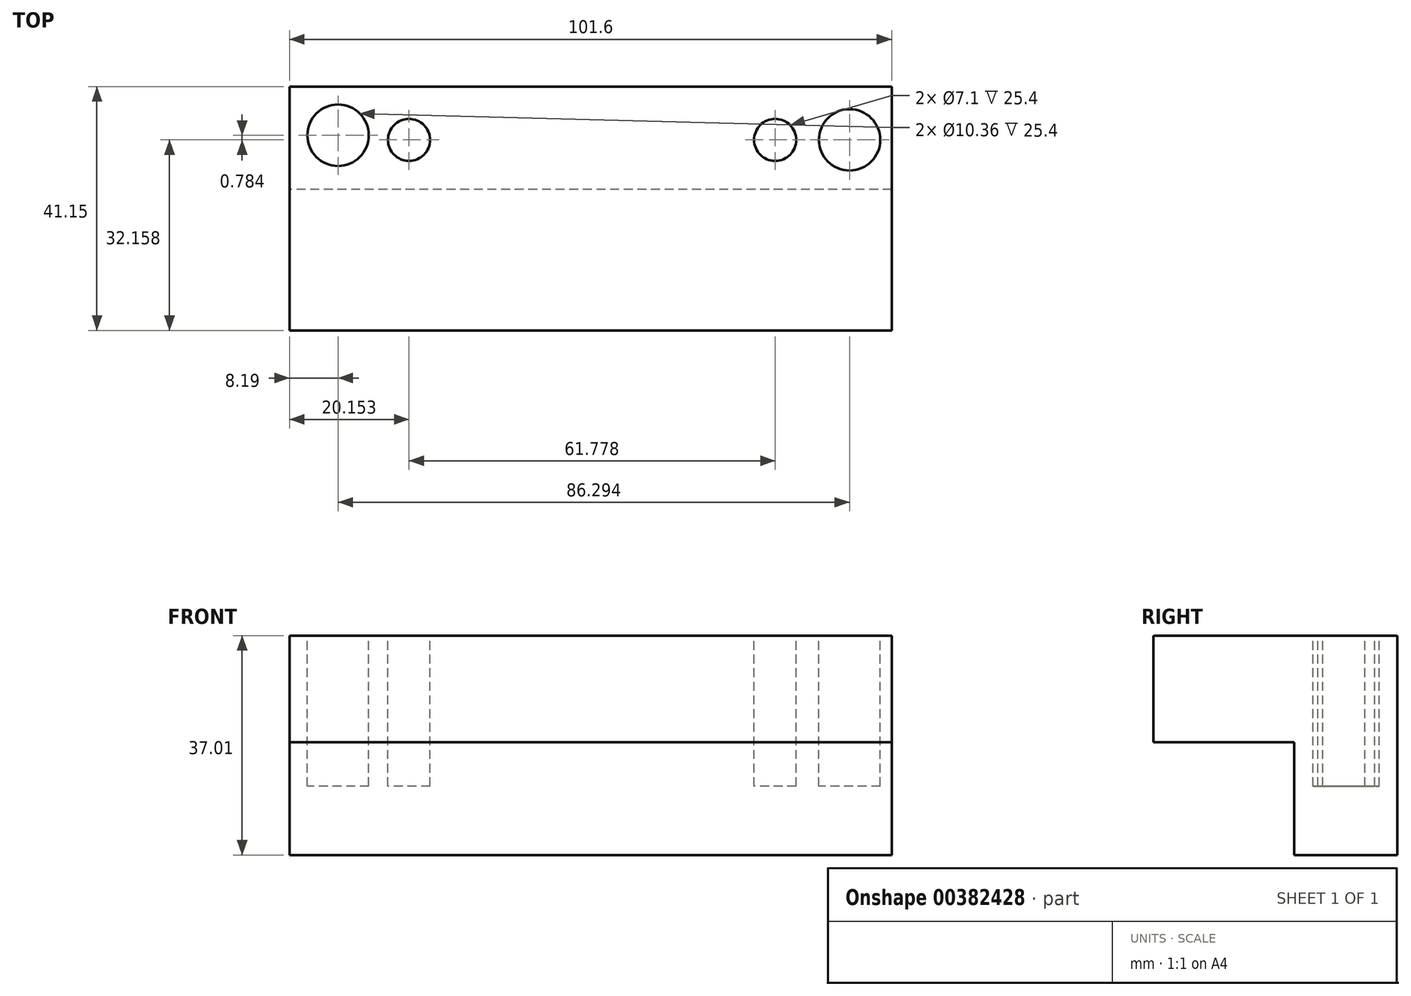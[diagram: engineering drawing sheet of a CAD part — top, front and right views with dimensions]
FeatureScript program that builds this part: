
annotation { "Feature Type Name" : "Feature", "Feature Type Description" : "" }
export const myFeature = defineFeature(function(context is Context, id is Id, definition is map)
    precondition{}
    {
        {
            var Q0;
            Q0=qCreatedBy(makeId("Right.planeOp"),FACE);
            var sketch = newSketch(context, id + "F0", { "sketchPlane" : qUnion([Q0])});
            skLineSegment(sketch, "E0", {"start": v(0, 0) * mm, "end": v(0, -19.05) * mm});
            skLineSegment(sketch, "E1", {"start": v(0, -19.05) * mm, "end": v(-17.37, -19.05) * mm});
            skLineSegment(sketch, "E2", {"start": v(-17.37, -19.05) * mm, "end": v(-17.37, 0) * mm});
            skLineSegment(sketch, "E3", {"start": v(-17.37, 0) * mm, "end": v(-41.15, 0) * mm});
            skLineSegment(sketch, "E4", {"start": v(-41.15, 0) * mm, "end": v(-41.15, 8.43) * mm});
            skLineSegment(sketch, "E5", {"start": v(-28.45, 17.96) * mm, "end": v(0, 17.96) * mm});
            skLineSegment(sketch, "E6", {"start": v(0, 14.78) * mm, "end": v(0, -6.55) * mm});
            skPoint(sketch, "E7.visualSharp", {"position": v(0, 17.96) * mm});
            skPoint(sketch, "E8.visualSharp", {"position": v(-41.15, 17.96) * mm});
            skLineSegment(sketch, "E9", {"start": v(0, 17.96) * mm, "end": v(0, 14.78) * mm});
            skLineSegment(sketch, "E10", {"start": v(0, 17.96) * mm, "end": v(0, 17.96) * mm});
            skLineSegment(sketch, "E11", {"start": v(-28.45, 17.96) * mm, "end": v(-41.15, 17.96) * mm});
            skLineSegment(sketch, "E12", {"start": v(-41.15, 8.43) * mm, "end": v(-41.15, 17.96) * mm});
            skSolve(sketch);
        }
        {
            var Q0;
            Q0 = qSketchRegion(id + "F0", true);
            extrude(context, id + "F1", {"entities" : qUnion([Q0]), "depth" : 101.6 * mm});
        }
        {
            var Q0;
            Q0=makeQuery(id+"F1.opExtrude","SWEPT_FACE",FACE,{"disambiguationData":[OSD([sQuery(id+"F0.wireOp",EDGE,"E5"),sQuery(id+"F0.wireOp",EDGE,"E11")])]});
            var sketch = newSketch(context, id + "F2", { "sketchPlane" : qUnion([Q0])});
            skCircle(sketch, "E13", {"center": v(8.19, -8.2) * mm, "radius": 5.18 * mm});
            skCircle(sketch, "E14", {"center": v(20.15, -9) * mm, "radius": 3.55 * mm});
            skCircle(sketch, "E15", {"center": v(94.48, -9) * mm, "radius": 5.18 * mm});
            skCircle(sketch, "E16", {"center": v(81.93, -9) * mm, "radius": 3.55 * mm});
            skSolve(sketch);
        }
        {
            var Q0;
            Q0 = qSketchRegion(id + "F2", true);
            extrude(context, id + "F3", {"entities" : qUnion([Q0]), "operationType" : NewBodyOperationType.REMOVE, "oppositeDirection" : true, "depth" : 25.4 * mm});
        }
    });
